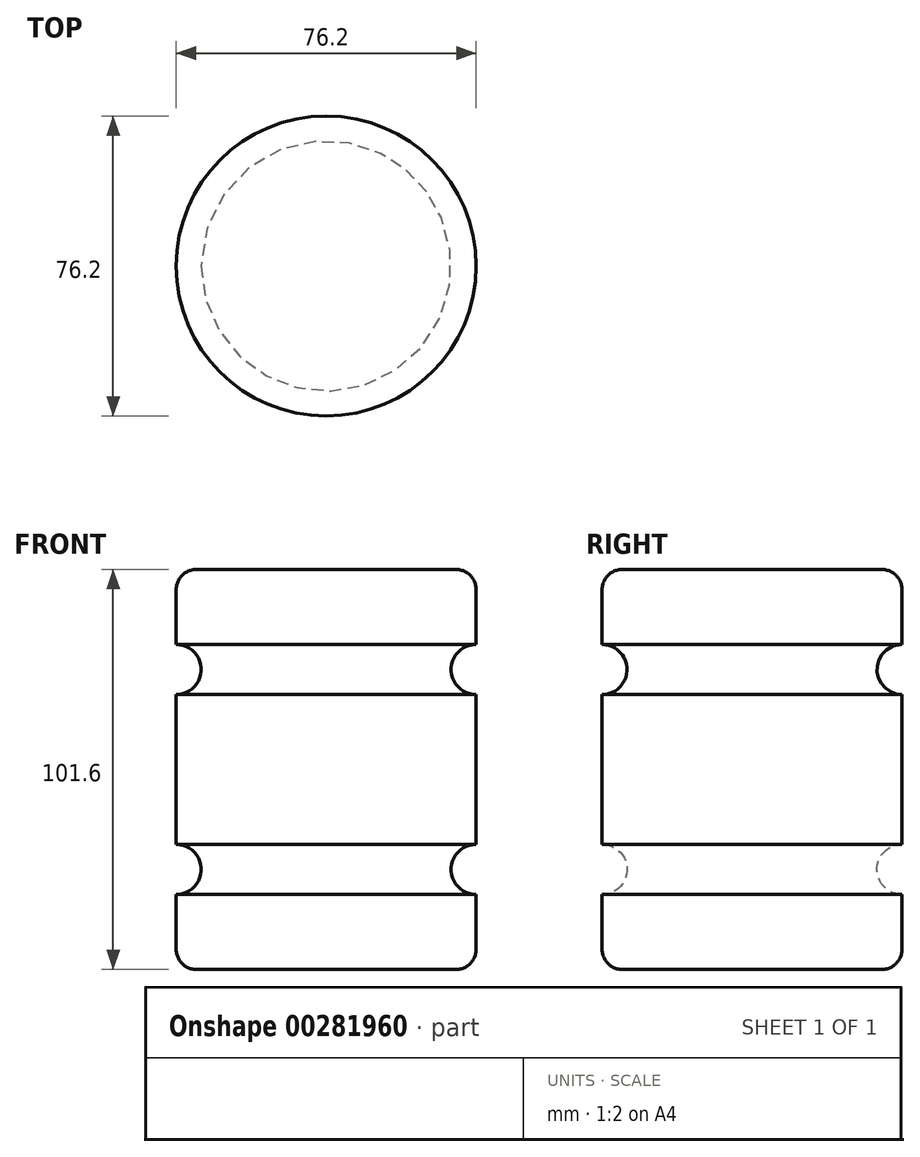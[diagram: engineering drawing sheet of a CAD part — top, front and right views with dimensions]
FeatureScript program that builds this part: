
annotation { "Feature Type Name" : "Feature", "Feature Type Description" : "" }
export const myFeature = defineFeature(function(context is Context, id is Id, definition is map)
    precondition{}
    {
        {
            var Q0;
            Q0=qCreatedBy(makeId("Front.planeOp"),FACE);
            var sketch = newSketch(context, id + "F0", { "sketchPlane" : qUnion([Q0])});
            skLineSegment(sketch, "E0.bottom", {"start": v(0, 0) * mm, "end": v(-38.1, 0) * mm});
            skLineSegment(sketch, "E0.top", {"start": v(0, 101.6) * mm, "end": v(-38.1, 101.6) * mm});
            skLineSegment(sketch, "E0.left", {"start": v(0, 0) * mm, "end": v(0, 19.05) * mm});
            skLineSegment(sketch, "E0.right", {"start": v(-38.1, 0) * mm, "end": v(-38.1, 101.6) * mm});
            skArc(sketch, "E1", {"start": v(0, 31.75) * mm, "mid": v(-6.35, 25.4) * mm, "end": v(0, 19.05) * mm});
            skArc(sketch, "E2", {"start": v(0, 82.55) * mm, "mid": v(-6.35, 76.2) * mm, "end": v(0, 69.85) * mm});
            skLineSegment(sketch, "E3.trimOffspring", {"start": v(0, 82.55) * mm, "end": v(0, 101.6) * mm});
            skLineSegment(sketch, "E4.trimOffspring", {"start": v(0, 31.75) * mm, "end": v(0, 69.85) * mm});
            skSolve(sketch);
        }
        {
            var Q0;
            Q0=makeQuery(id+"F0.imprint","IMPRINT",FACE,{"disambiguationData":[TD([[makeQuery(id+"F0.imprint","IMPRINT",EDGE,{"derivedFrom":sQuery(id+"F0.wireOp",EDGE,"E0.bottom")}),-1.0]])]});
            var Q1;
            Q1=sQuery(id+"F0.wireOp",EDGE,"E0.right");
            revolve(context, id + "F1", {"entities" : qUnion([Q0]), "axis" : qUnion([Q1]), "revolveType" : RevolveType.FULL});
        }
        {
            var Q0;
            Q0=makeQuery(id+"F1.opRevolve","SWEPT_EDGE",EDGE,{"disambiguationData":[OSD([sQuery(id+"F0.wireOp",EDGE,"E0.top"),sQuery(id+"F0.wireOp",EDGE,"E3.trimOffspring")])]});
            var Q1;
            Q1=makeQuery(id+"F1.opRevolve","SWEPT_EDGE",EDGE,{"disambiguationData":[OSD([sQuery(id+"F0.wireOp",EDGE,"E0.bottom"),sQuery(id+"F0.wireOp",EDGE,"E0.left")])]});
            fillet(context, id + "F2", {"entities" : qUnion([Q0, Q1]), "radius" : 5.08 * mm, "tangentPropagation" : true, "allowEdgeOverflow" : false});
        }
    });
